# Revit family: Pump_Commercial-Sewage_Dewatering-Zoeller-X64HD_Single_Seal_4-HH-50-60BHP_Series
name_source: partatom
category: Mechanical Equipment
revit_build: Autodesk Revit 2014 (Build: 20130308_1515(x64)
units: mm (PartAtom-declared; Revit-internal decimal feet)

## types (4) — shared parameters
Assembly Code = D2090
Connection Description = 4" Horizontal Discharge
Default Elevation = 0"
Description = Heavy Duty Solids-Handling Pumps
Discharge Diameter = 4"
Discharge Radius = 2"
Flange = ANSI B16.1 CLASS 125
Height = 55 19/32"
Hertz = 60
High Temperature (5-10 BHP) = No
Impeller Type = 2 Vane Enclosed
Installation Type = Floor Mounted
Insulation = Class F
Inverted Duty = No
Inverted Duty Submersible = No
Length = 25 5/8"
Manufacturer = Zoeller
Material = Cast Iron-Zoeller-Powder Coated Epoxy
Max. Flow @ 45' = 0 GPM
Max. Flow @ 60' = 0 GPM
Max. Flow @ 85' = 0 GPM
Max. Stator Temp. = 311 °F
Max. Water Temp. = 104 °F
Min. Recommended Fluid Level = 36"
Moisture Detection = Moisture Sensing Probes
Motor Design Letter = NEMA B
Motor Shaft = 416 SS
Motor Thermal Shutoff = Thermal Sensors With Automatic Reset
Motor Type = Standard Submersible
NEC Locked Rotor Code = G
O-Rings (Optional) Viton = No
O-Rings and Cover Gasket = Buna-N
Operation = Non-Automatic
Phase = 3
Power Cord = 25' (7.6 m) #2-4 SO
Price = Prices may vary. Please consult Manufacturer Representative for most up-to-date price list.
Product Documentation Link = https://www.zoellerengprod.com
Product Page URL = https://www.zoellerengprod.com
RPM = 1725
Sensor Cord Size = #16-5 SO
Service Factor = 1.15
Shaft Seal (Standard) = Carbon/Ceramic
Shaft Seal Lower (Options) = Silicon Carbide
Shaft Seal Upper (Options) = Silicon Carbide
Solid Size = 4"- 3-1/8"
Tandem Seals = Standard
Trimmed Impeller = No
URL = http://www.zoellerpumps.com
Warranty Information = 36 Months (Limited)
Waste Connection = Yes
Width = 22 1/2"

## per-type parameters (varying)
| type | Amps | Apparent Load | Flow Rate | Impeller Diameter | Locked Rotor Amps (Voltage Dependant) | Max. Flow @ 117' | Max. Flow @ 135' | Max. Head | Maximum KW Input | Model | Motor | Pump Net Weight: lbs. (kg) | Voltage |
| X6427 - 460V/3Ph/64.3A/50BHP | 64 A | 29578 VA | 840 GPM | 12 1/8" | 362 | 840 GPM | 0 GPM | 165' | 40.9 | X6427 | 50 BHP | 1050 lbs. (476 kg) | 460 V |
| X6428 - 460V/3Ph/74.9A/60BHP | 75 A | 34454 VA | 940 GPM | 12 7/8" | 415 | 0 GPM | 940 GPM | 195' | 51.4 | X6428 | 60 BHP | 1100 lbs. (499 kg) | 460 V |
| X6427 - 575V/3Ph/51.4A/50BHP | 51 A | 29555 VA | 840 GPM | 12 1/8" | 290 | 840 GPM | 0 GPM | 165' | 40.9 | X6427 | 50 BHP | 1050 lbs. (476 kg) | 575 V |
| X6428 - 575V/3Ph/59.9A/60BHP | 60 A | 34443 VA | 940 GPM | 12 7/8" | 332 | 0 GPM | 940 GPM | 195' | 51.4 | X6428 | 60 BHP | 1100 lbs. (499 kg) | 575 V |

## geometry (parser evidence)
native form markers: Sweep x3
no freeform markers — native parametric forms only
